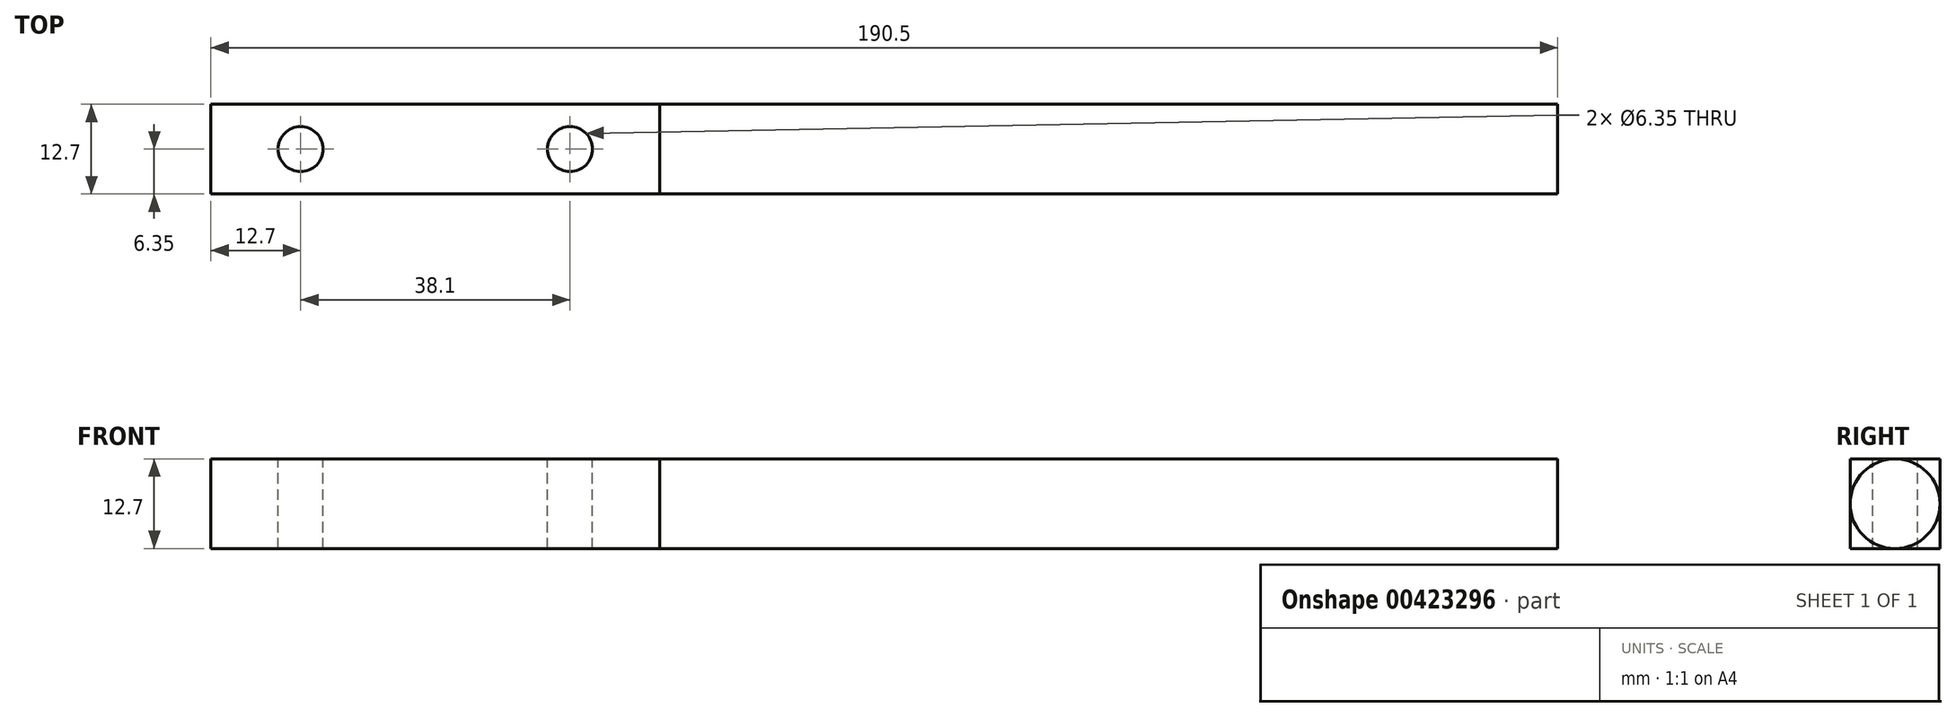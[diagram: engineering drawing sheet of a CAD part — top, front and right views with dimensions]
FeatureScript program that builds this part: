
annotation { "Feature Type Name" : "Feature", "Feature Type Description" : "" }
export const myFeature = defineFeature(function(context is Context, id is Id, definition is map)
    precondition{}
    {
        {
            var Q0;
            Q0=qCreatedBy(makeId("Front.planeOp"),FACE);
            var sketch = newSketch(context, id + "F0", { "sketchPlane" : qUnion([Q0])});
            skLineSegment(sketch, "E0.bottom", {"start": v(0, -6.35) * mm, "end": v(-63.5, -6.35) * mm});
            skLineSegment(sketch, "E0.top", {"start": v(0, 6.35) * mm, "end": v(-63.5, 6.35) * mm});
            skLineSegment(sketch, "E0.left", {"start": v(0, -6.35) * mm, "end": v(0, 6.35) * mm});
            skLineSegment(sketch, "E0.right", {"start": v(-63.5, -6.35) * mm, "end": v(-63.5, 6.35) * mm});
            skSolve(sketch);
        }
        {
            var Q0;
            Q0 = qSketchRegion(id + "F0", true);
            extrude(context, id + "F1", {"entities" : qUnion([Q0]), "endBound" : BoundingType.SYMMETRIC, "depth" : 12.7 * mm});
        }
        {
            var Q0;
            Q0=makeQuery(id+"F1.opExtrude","SWEPT_FACE",FACE,{"disambiguationData":[OSD([sQuery(id+"F0.wireOp",EDGE,"E0.left")])]});
            var sketch = newSketch(context, id + "F2", { "sketchPlane" : qUnion([Q0])});
            skCircle(sketch, "E1", {"center": v(0, 0) * mm, "radius": 6.35 * mm});
            skSolve(sketch);
        }
        {
            var Q0;
            Q0 = qSketchRegion(id + "F2", true);
            extrude(context, id + "F3", {"entities" : qUnion([Q0]), "operationType" : NewBodyOperationType.ADD, "depth" : 127 * mm});
        }
        {
            var Q0;
            Q0=makeQuery(id+"F1.opExtrude","SWEPT_FACE",FACE,{"disambiguationData":[OSD([sQuery(id+"F0.wireOp",EDGE,"E0.top")])]});
            var sketch = newSketch(context, id + "F4", { "sketchPlane" : qUnion([Q0])});
            skCircle(sketch, "E2", {"center": v(-50.8, 0) * mm, "radius": 3.18 * mm});
            skCircle(sketch, "E3", {"center": v(-12.7, 0) * mm, "radius": 3.18 * mm});
            skSolve(sketch);
        }
        {
            var Q0;
            Q0 = qSketchRegion(id + "F4", true);
            extrude(context, id + "F5", {"entities" : qUnion([Q0]), "operationType" : NewBodyOperationType.REMOVE, "endBound" : BoundingType.THROUGH_ALL, "oppositeDirection" : true, "depth" : 25.4 * mm});
        }
    });
